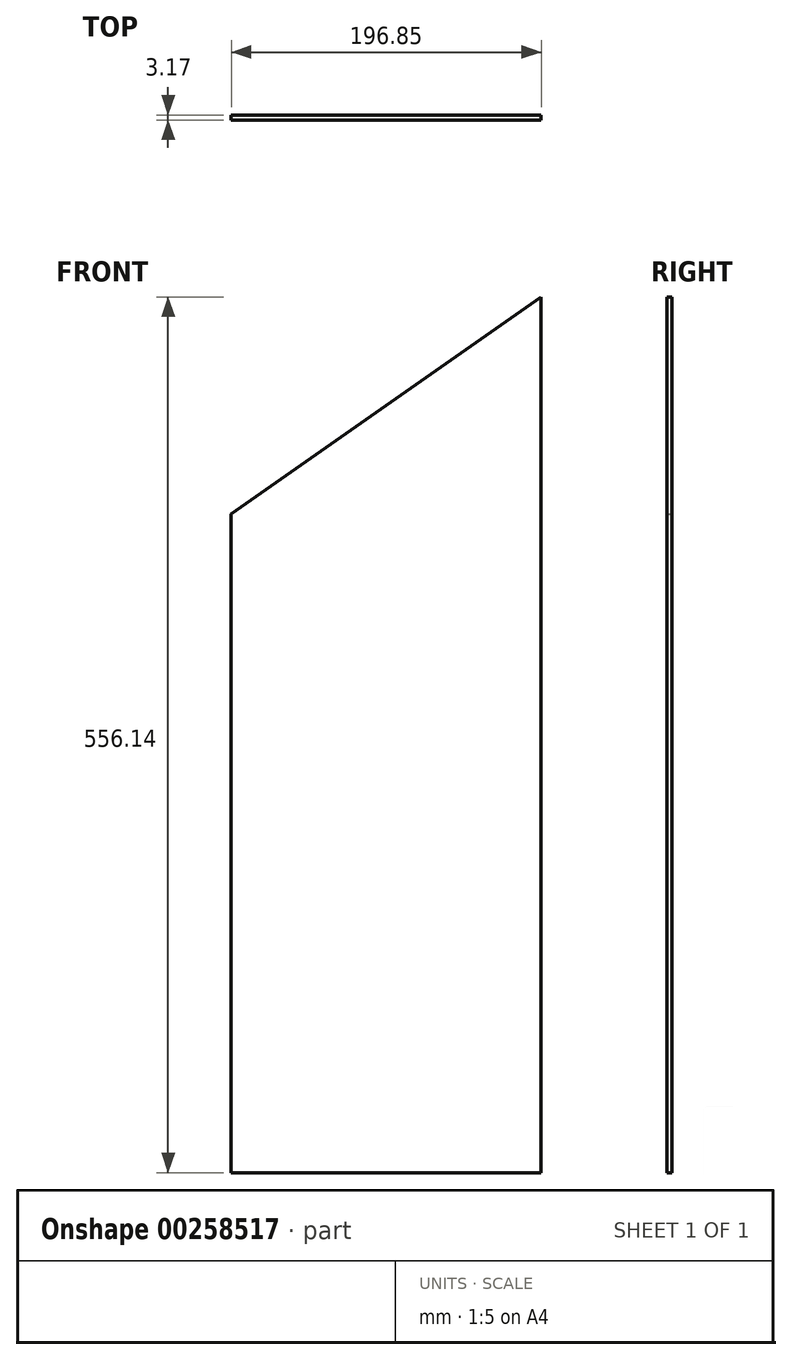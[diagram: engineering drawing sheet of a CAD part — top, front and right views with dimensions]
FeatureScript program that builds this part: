
annotation { "Feature Type Name" : "Feature", "Feature Type Description" : "" }
export const myFeature = defineFeature(function(context is Context, id is Id, definition is map)
    precondition{}
    {
        {
            var Q0;
            Q0=qCreatedBy(makeId("Front.planeOp"),FACE);
            var sketch = newSketch(context, id + "F0", { "sketchPlane" : qUnion([Q0])});
            skLineSegment(sketch, "E0.top", {"start": v(98.42, -278.07) * mm, "end": v(-98.43, -278.07) * mm});
            skLineSegment(sketch, "E0.left", {"start": v(98.43, 278.07) * mm, "end": v(98.42, -278.07) * mm});
            skLineSegment(sketch, "E0.right", {"start": v(-98.42, 140.24) * mm, "end": v(-98.43, -278.07) * mm});
            skPoint(sketch, "E0.middle", {"position": v(0, 0) * mm});
            skLineSegment(sketch, "E1", {"start": v(98.42, 278.07) * mm, "end": v(-98.43, 140.24) * mm});
            skPoint(sketch, "E2.orphan", {"position": v(-98.43, 278.07) * mm});
            skSolve(sketch);
        }
        {
            var Q0;
            Q0 = qSketchRegion(id + "F0", true);
            extrude(context, id + "F1", {"entities" : qUnion([Q0]), "depth" : 3.17 * mm});
        }
    });
